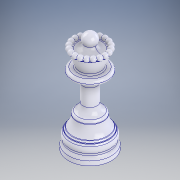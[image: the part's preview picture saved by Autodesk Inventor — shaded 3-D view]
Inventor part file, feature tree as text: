
AUTODESK INVENTOR PART (.ipt)
format: ipt  version: 2018 (Build 220112000, 112)  size: 1,009,152 bytes
history: native  units: in
note: dims shown in document units (in); Inventor stores cm internally (conversion verified against a paired STEP export)
features: fillet x16, sketch x10, extrude x8, chamfer x2, revolve x2, draft x1, plane x1, pattern_circular x1
ambient origin geometry x8: Origin, YZ Plane, XZ Plane, XY Plane, X Axis, Y Axis, Z Axis, Center Point
bodies: Solid1 (feature_tree)
feature tree (41):
  extrude  "Extrusion1"  Depth=0.2in TaperAngle=0.0deg
  fillet  "Fillet1"  Radius=0.1in
  extrude  "Extrusion2"  Depth=0.1in
  fillet  "Fillet2"  Radius=0.025in
  fillet  "Fillet3"  Radius=0.096in
  chamfer  "Chamfer1"  Distance=0.0625in
  extrude  "Extrusion3"  Depth=0.125in
  chamfer  "Chamfer2"  Distance=0.2835in
  fillet  "Fillet4"  Radius=0.375in
  fillet  "Fillet5"  Radius=0.0625in
  fillet  "Fillet6"  Radius=0.33in
  extrude  "Extrusion4"  Depth=0.1875in
  fillet  "Fillet7"  Radius=0.125in
  fillet  "Fillet8"  Radius=0.1875in
  extrude  "Extrusion5"  Depth=0.475in
  fillet  "Fillet9"  Radius=0.375in
  extrude  "Extrusion6"  Depth=0.0225in
  fillet  "Fillet10"  Radius=0.0225in
  fillet  "Fillet11"  Radius=0.025in
  extrude  "Extrusion7"  TaperAngle=90.0deg  [1 undecoded]
  draft  "FaceDraft1"
  fillet  "Fillet12"  Radius=7.874in
  fillet  "Fillet13"  Radius=0.1875in
  plane  "Work Plane1"
  revolve  "Revolution1"  [1 undecoded]
  pattern_circular  "Circular Pattern1"  Angle=90.0deg  [1 undecoded]
  extrude  "Extrusion11"  Depth=0.15in
  fillet  "Fillet15"  Radius=0.025in
  fillet  "Fillet16"  [1 undecoded]
  revolve  "Revolution2"  [1 undecoded]
  fillet  "Fillet17"  [1 undecoded]
  sketch  "Sketch1"  dims[d0=1.0in d1=0.2in d2=0.0in d3=0.1in]
  sketch  "Sketch2"  dims[d4=0.2in d5=0.0in d6=0.1in d7=0.025in]
  sketch  "Sketch3"  dims[d8=0.0625in d9=0.125in d10=0.3917in d11=0.096in d12=0.0in d13=0.0625in d14=0.125in d15=0.3779in]
  sketch  "Sketch4"  dims[d16=0.025in d17=0.125in]
  sketch  "Sketch5"  dims[d18=0.125in d19=0.2835in d20=0.0in d21=0.375in d22=0.0625in d23=0.33in]
  sketch  "Sketch6"  dims[d24=0.75in d25=0.0in d26=0.1875in d27=0.125in d28=0.0in d29=0.1875in]
  sketch  "Sketch7"  dims[d30=0.0625in d31=0.475in d32=0.375in d33=0.0in]
  sketch  "Sketch11"  dims[d34=-0.1374in d44=0.0225in d45=0.0225in d50=0.025in]
  sketch  "Sketch12"  dims[d51=0.125in d52=90.0deg d53=7.874in d54=360.0deg d56=0.1875in d57=0.0in]
  sketch  "Sketch13"  dims[d58=0.1in d59=0.1625in d60=90.0deg d61=0.15in d62=0.025in]
note: 6 required parameter values undecoded (feature->parameter linkage not recoverable at this tier; creation-order binding heuristic only, values carry confidence <= 0.55)